# Revit family: TowelRail_SurfaceMount_Abey_Vela_Single
name_source: partatom
category: Specialty Equipment
units: mm (PartAtom-declared; Revit-internal decimal feet)

## family parameters
Always vertical = Yes
Cut with Voids When Loaded = No
OmniClass Number = 23.31.25.25
OmniClass Title = Towel Bars
Part Type = Normal
Room Calculation Point = No
Round Connector Dimension = Use Diameter
Shared = No
Work Plane-Based = No

## types (10) — shared parameters
Assembly Code = C1030210
IfcExportAs = IfcFurniture
IfcExportType = NOTDEFINED
Manufacturer = Abey
ManufacturerOverallDepth = 65 mm  [stored 0.213255 ft]
ManufacturerOverallHeight = 25 mm  [stored 0.082021 ft]
ManufacturerURLProductSpecific = https://www.abey.com.au
ModifiedIssue = 20241025 $
URL = https://www.abey.com.au
Uniclass2015Code = Pr_40_20_76_90
Uniclass2015Title = Towel rails
Uniclass2015Version = Products v1.33
zero-valued in all types: Default Elevation

## per-type parameters (varying)
| type | Description | ManufacturerOverallWidth | ManufacturerSpecCode | Material | Model | Type Comments |
| Chrome (VSTR250) | Vela Single Towel Rail Chrome 250mm | 280 mm  [stored 0.918635 ft] | VSTR250 | Metal_Abey_Chrome | VSTR250 | Chrome |
| Black (VSTR250-B) | Vela Single Towel Rail Black 250mm | 280 mm  [stored 0.918635 ft] | VSTR250-B | Metal_Abey_Black | VSTR250-B | Black |
| Brushed Brass (VSTR250-BB) | Vela Single Towel Rail Brushed Brass 250mm | 280 mm  [stored 0.918635 ft] | VSTR250-BB | Metal_Abey_Brass | VSTR250-BB | Brushed Brass |
| Gun Metal (VSTR250-GM) | Vela Single Towel Rail Gun Metal 250mm | 280 mm  [stored 0.918635 ft] | VSTR250-GM | Metal_Abey_GunMetal | VSTR250-GM | Gun Metal |
| Brushed Nickel (VSTR250-BN) | Vela Single Towel Rail Brushed Nickel 250mm | 280 mm  [stored 0.918635 ft] | VSTR250-BN | Metal_Abey_BrushedNickel | VSTR250-BN | Brushed Nickel |
| Chrome (VSTR600) | Vela Single Towel Rail Chrome 600mm | 630 mm  [stored 2.06693 ft] | VSTR600 | Metal_Abey_Chrome | VSTR600 | Chrome |
| Black (VSTR600-B) | Vela Single Towel Rail Black 600mm | 630 mm  [stored 2.06693 ft] | VSTR600-B | Metal_Abey_Black | VSTR600-B | Black |
| Brushed Brass (VSTR600-BB) | Vela Single Towel Rail Brushed Brass 600mm | 630 mm  [stored 2.06693 ft] | VSTR600-BB | Metal_Abey_Brass | VSTR600-BB | Brushed Brass |
| Gun Metal (VSTR600-GM) | Vela Single Towel Rail Gun Metal 600mm | 630 mm  [stored 2.06693 ft] | VSTR600-GM | Metal_Abey_GunMetal | VSTR600-GM | Gun Metal |
| Brushed Nickel (VSTR600-BN) | Vela Single Towel Rail Brushed Nickel 600mm | 630 mm  [stored 2.06693 ft] | VSTR600-BN | Metal_Abey_BrushedNickel | VSTR600-BN | Brushed Nickel |

note: [stored X ft] marks values corroborated as IEEE doubles in the binary element streams (Revit-internal decimal feet)

## geometry (parser evidence)
native form markers: Sweep x2
no freeform markers — native parametric forms only
